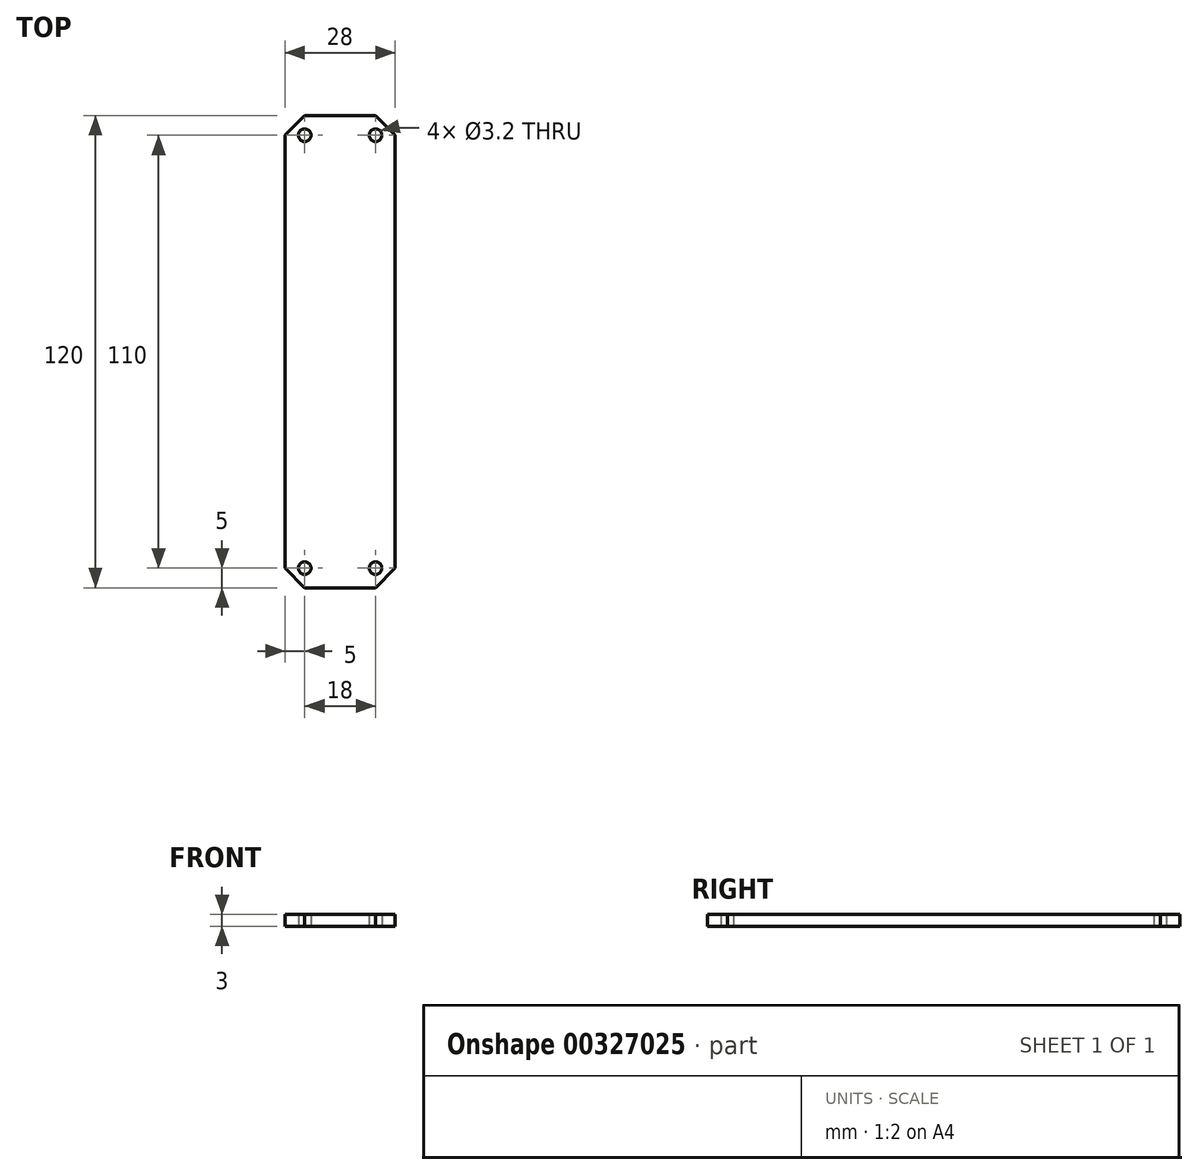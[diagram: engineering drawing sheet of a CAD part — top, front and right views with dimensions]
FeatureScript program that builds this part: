
annotation { "Feature Type Name" : "Feature", "Feature Type Description" : "" }
export const myFeature = defineFeature(function(context is Context, id is Id, definition is map)
    precondition{}
    {
        {
            var Q0;
            Q0=qCreatedBy(makeId("Top.planeOp"),FACE);
            var sketch = newSketch(context, id + "F0", { "sketchPlane" : qUnion([Q0])});
            skLineSegment(sketch, "E0.bottom", {"start": v(14, 60) * mm, "end": v(-14, 60) * mm});
            skLineSegment(sketch, "E0.top", {"start": v(14, -60) * mm, "end": v(-14, -60) * mm});
            skLineSegment(sketch, "E0.left", {"start": v(14, 60) * mm, "end": v(14, -60) * mm});
            skLineSegment(sketch, "E0.right", {"start": v(-14, 60) * mm, "end": v(-14, -60) * mm});
            skPoint(sketch, "E0.middle", {"position": v(0, 0) * mm});
            skCircle(sketch, "E1", {"center": v(9, 55) * mm, "radius": 1.6 * mm});
            skCircle(sketch, "E2", {"center": v(9, -55) * mm, "radius": 1.6 * mm});
            skCircle(sketch, "E3.MirrorC", {"center": v(-9, 55) * mm, "radius": 1.6 * mm});
            skCircle(sketch, "E4.MirrorC", {"center": v(-9, -55) * mm, "radius": 1.6 * mm});
            skSolve(sketch);
        }
        {
            var Q0;
            Q0 = qSketchRegion(id + "F0", true);
            extrude(context, id + "F1", {"entities" : qUnion([Q0]), "depth" : 3 * mm});
        }
        {
            var Q0;
            Q0=makeQuery(id+"F1.opExtrude","SWEPT_EDGE",EDGE,{"disambiguationData":[OSD([sQuery(id+"F0.wireOp",EDGE,"E0.bottom"),sQuery(id+"F0.wireOp",EDGE,"E0.right")])]});
            var Q1;
            Q1=makeQuery(id+"F1.opExtrude","SWEPT_EDGE",EDGE,{"disambiguationData":[OSD([sQuery(id+"F0.wireOp",EDGE,"E0.bottom"),sQuery(id+"F0.wireOp",EDGE,"E0.left")])]});
            var Q2;
            Q2=makeQuery(id+"F1.opExtrude","SWEPT_EDGE",EDGE,{"disambiguationData":[OSD([sQuery(id+"F0.wireOp",EDGE,"E0.top"),sQuery(id+"F0.wireOp",EDGE,"E0.right")])]});
            var Q3;
            Q3=makeQuery(id+"F1.opExtrude","SWEPT_EDGE",EDGE,{"disambiguationData":[OSD([sQuery(id+"F0.wireOp",EDGE,"E0.top"),sQuery(id+"F0.wireOp",EDGE,"E0.left")])]});
            chamfer(context, id + "F2", {"entities" : qUnion([Q0, Q1, Q2, Q3]), "width" : 5 * mm, "tangentPropagation" : true});
        }
    });
